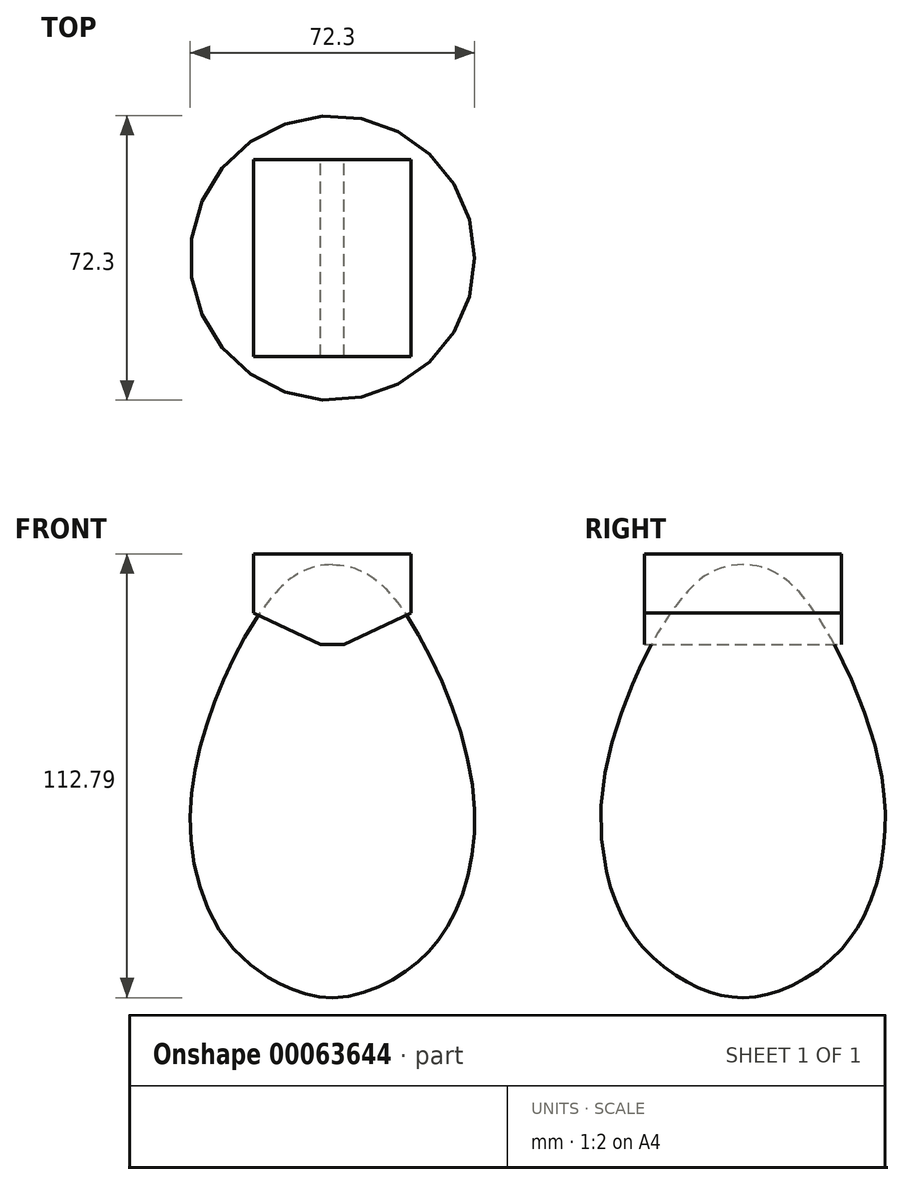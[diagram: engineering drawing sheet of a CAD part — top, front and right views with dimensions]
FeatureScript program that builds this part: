
annotation { "Feature Type Name" : "Feature", "Feature Type Description" : "" }
export const myFeature = defineFeature(function(context is Context, id is Id, definition is map)
    precondition{}
    {
        {
            var Q0;
            Q0=qCreatedBy(makeId("Front.planeOp"),FACE);
            var sketch = newSketch(context, id + "F0", { "sketchPlane" : qUnion([Q0])});
            skFitSpline(sketch, "E0", {"points": [v(0, 43.71) * mm, v(16, 34.71) * mm, v(35.5, -12) * mm, v(30.5, -46) * mm, v(18, -60) * mm, v(0, -66.29) * mm], "startDerivative": vector(119, -2.1) * mm, "endDerivative": vector(-116.3, 0) * mm});
            skLineSegment(sketch, "E1", {"start": v(0, -66.29) * mm, "end": v(0, 43.71) * mm});
            skSolve(sketch);
        }
        {
            var Q0;
            Q0 = qSketchRegion(id + "F0", true);
            var Q1;
            Q1=sQuery(id+"F0.wireOp",EDGE,"E1");
            revolve(context, id + "F1", {"entities" : qUnion([Q0]), "axis" : qUnion([Q1]), "revolveType" : RevolveType.FULL});
        }
        {
            var Q0;
            Q0=qCreatedBy(makeId("Front.planeOp"),FACE);
            var sketch = newSketch(context, id + "F2", { "sketchPlane" : qUnion([Q0])});
            skLineSegment(sketch, "E2", {"start": v(0, 23.5) * mm, "end": v(3, 23.5) * mm});
            skLineSegment(sketch, "E3", {"start": v(3, 23.5) * mm, "end": v(20, 31.5) * mm});
            skLineSegment(sketch, "E4", {"start": v(20, 31.5) * mm, "end": v(20, 46.5) * mm});
            skLineSegment(sketch, "E5", {"start": v(20, 46.5) * mm, "end": v(0, 46.5) * mm});
            skLineSegment(sketch, "E6", {"start": v(0, 46.5) * mm, "end": v(0, 23.5) * mm});
            skLineSegment(sketch, "E7.MirrorCS", {"start": v(-20, 46.5) * mm, "end": v(0, 46.5) * mm});
            skLineSegment(sketch, "E8.MirrorCS", {"start": v(-20, 31.5) * mm, "end": v(-20, 46.5) * mm});
            skLineSegment(sketch, "E9.MirrorCS", {"start": v(-3, 23.5) * mm, "end": v(-20, 31.5) * mm});
            skLineSegment(sketch, "E10.MirrorCS", {"start": v(0, 23.5) * mm, "end": v(-3, 23.5) * mm});
            skSolve(sketch);
        }
        {
            var Q0;
            Q0 = qSketchRegion(id + "F2", true);
            extrude(context, id + "F3", {"entities" : qUnion([Q0]), "depth" : 25 * mm, "hasSecondDirection" : true, "secondDirectionOppositeDirection" : true, "secondDirectionDepth" : 25 * mm});
        }
    });
